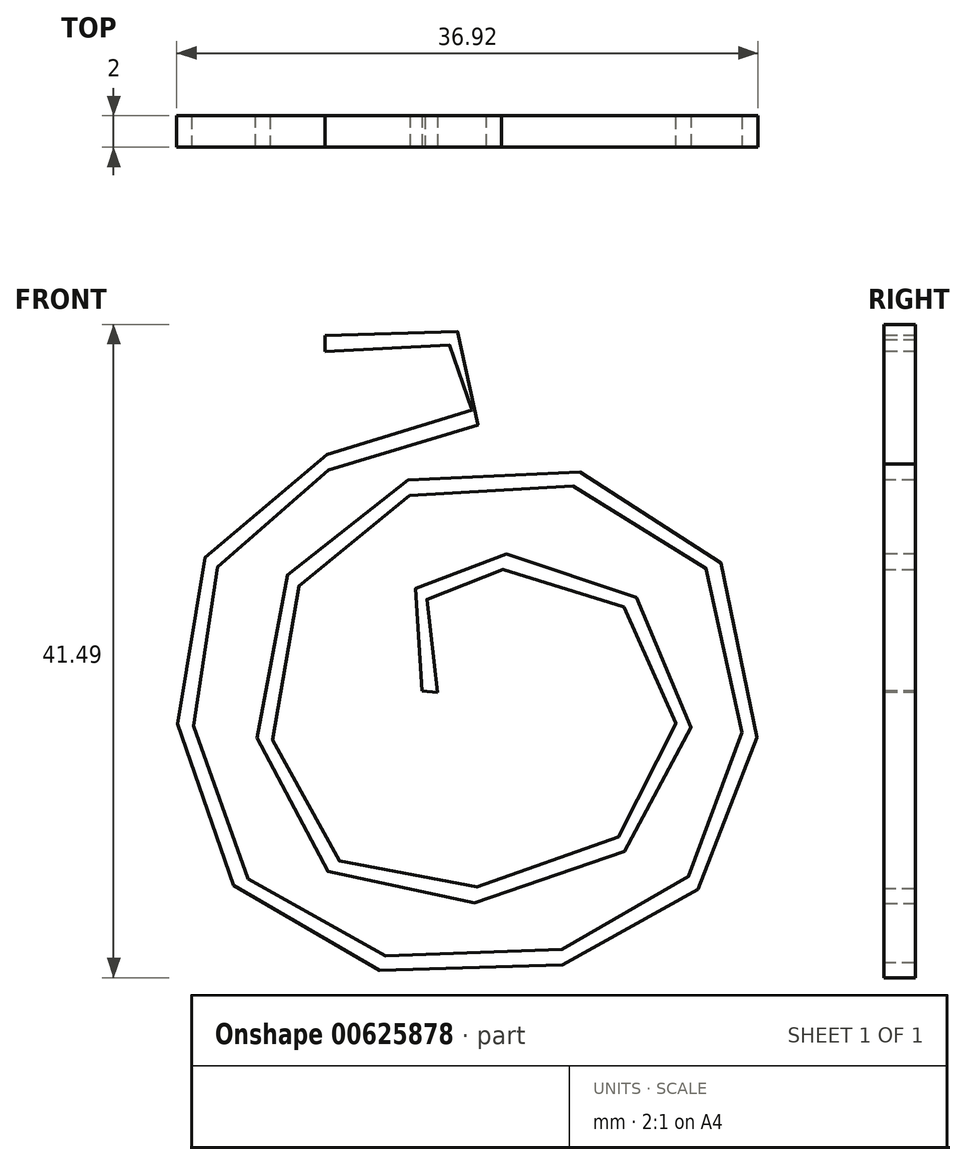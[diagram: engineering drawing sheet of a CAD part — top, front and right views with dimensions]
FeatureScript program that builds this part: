
annotation { "Feature Type Name" : "Feature", "Feature Type Description" : "" }
export const myFeature = defineFeature(function(context is Context, id is Id, definition is map)
    precondition{}
    {
        {
            var Q0;
            Q0=qCreatedBy(makeId("Front.planeOp"),FACE);
            var sketch = newSketch(context, id + "F0", { "sketchPlane" : qUnion([Q0])});
            skFitSpline(sketch, "E0", {"points": [v(0, 0) * mm, v(8.79, 0) * mm, v(9.9, -3.23) * mm, v(-2.75, -7.79) * mm, v(-9.42, -21.36) * mm, v(-2.97, -36.7) * mm, v(15.68, -38.82) * mm, v(26.17, -30.03) * mm, v(24.36, -12.35) * mm, v(8.12, -7.45) * mm, v(-3.2, -15.8) * mm, v(-1.86, -31.14) * mm, v(10.38, -34.92) * mm, v(22.17, -28.25) * mm, v(20.83, -16.68) * mm, v(10.6, -12.9) * mm, v(5.7, -15.13) * mm, v(6.15, -21.58) * mm], "startDerivative": vector(177.3, 40.27) * mm, "endDerivative": vector(31.08, -233.1) * mm});
            skSolve(sketch);
        }
        {
            var Q0;
            Q0=qCreatedBy(makeId("Right.planeOp"),FACE);
            var sketch = newSketch(context, id + "F1", { "sketchPlane" : qUnion([Q0])});
            skLineSegment(sketch, "E1.bottom", {"start": v(1, 0) * mm, "end": v(-1, 0) * mm});
            skLineSegment(sketch, "E1.top", {"start": v(1, 1) * mm, "end": v(-1, 1) * mm});
            skLineSegment(sketch, "E1.left", {"start": v(1, 0) * mm, "end": v(1, 1) * mm});
            skLineSegment(sketch, "E1.right", {"start": v(-1, 0) * mm, "end": v(-1, 1) * mm});
            skSolve(sketch);
        }
        {
            var Q0;
            Q0=makeQuery(id+"F1.imprint","IMPRINT",FACE,{"disambiguationData":[TD([[makeQuery(id+"F1.imprint","IMPRINT",EDGE,{"derivedFrom":sQuery(id+"F1.wireOp",EDGE,"E1.bottom")}),-1.0]])]});
            var Q1;
            Q1=sQuery(id+"F0.wireOp",EDGE,"E0");
            sweep(context, id + "F2", {"profiles" : qUnion([Q0]), "path" : qUnion([Q1])});
        }
    });
